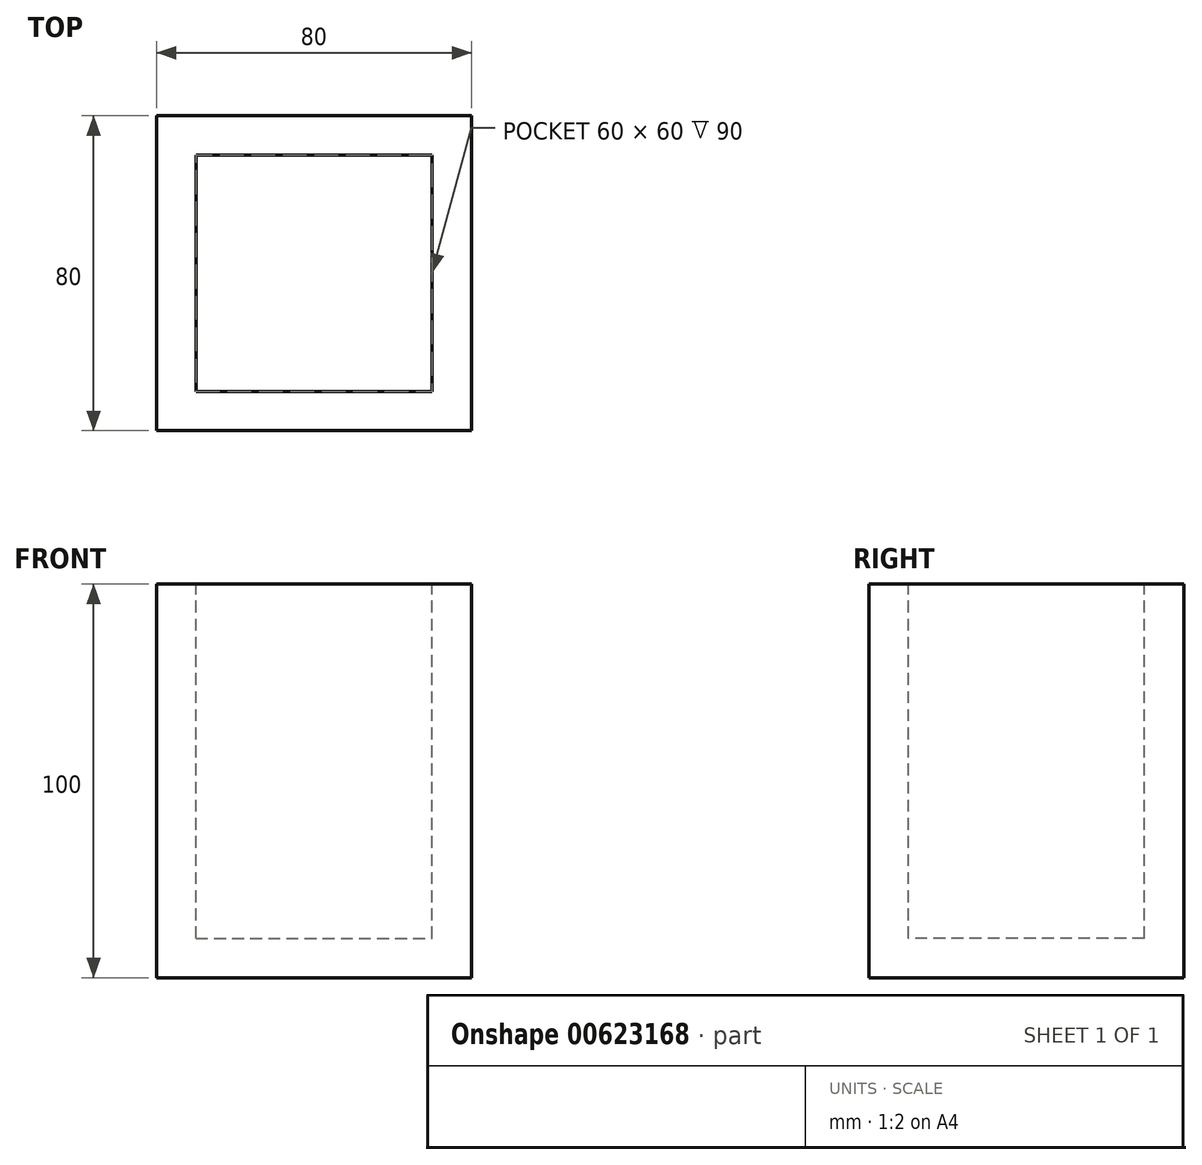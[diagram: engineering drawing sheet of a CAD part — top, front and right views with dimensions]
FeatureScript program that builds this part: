
annotation { "Feature Type Name" : "Feature", "Feature Type Description" : "" }
export const myFeature = defineFeature(function(context is Context, id is Id, definition is map)
    precondition{}
    {
        {
            var Q0;
            Q0=qCreatedBy(makeId("Top.planeOp"),FACE);
            var sketch = newSketch(context, id + "F0", { "sketchPlane" : qUnion([Q0])});
            skLineSegment(sketch, "E0", {"start": v(0, 0) * mm, "end": v(0, 80) * mm});
            skLineSegment(sketch, "E1", {"start": v(0, 80) * mm, "end": v(-80, 80) * mm});
            skLineSegment(sketch, "E2", {"start": v(-80, 80) * mm, "end": v(-80, 0) * mm});
            skLineSegment(sketch, "E3", {"start": v(-80, 0) * mm, "end": v(0, 0) * mm});
            skSolve(sketch);
        }
        {
            var Q0;
            Q0 = qSketchRegion(id + "F0", true);
            extrude(context, id + "F1", {"entities" : qUnion([Q0]), "depth" : 100 * mm, "offsetDistance" : 25 * mm});
        }
        {
            var Q0;
            Q0=makeQuery(id+"F1.opExtrude","CAP_FACE",FACE,{"disambiguationData":[OSD([sQuery(id+"F0.wireOp",EDGE,"E0"),sQuery(id+"F0.wireOp",EDGE,"E1"),sQuery(id+"F0.wireOp",EDGE,"E2"),sQuery(id+"F0.wireOp",EDGE,"E3")])],"isStart":false});
            var sketch = newSketch(context, id + "F2", { "sketchPlane" : qUnion([Q0])});
            skPoint(sketch, "E4", {"position": v(-70, 70) * mm});
            skPoint(sketch, "E5", {"position": v(-10, 70) * mm});
            skPoint(sketch, "E6", {"position": v(-10, 10) * mm});
            skPoint(sketch, "E7", {"position": v(-70, 10) * mm});
            skLineSegment(sketch, "E8", {"start": v(-70, 70) * mm, "end": v(-10, 70) * mm});
            skLineSegment(sketch, "E9", {"start": v(-10, 10) * mm, "end": v(-70, 10) * mm});
            skLineSegment(sketch, "E10", {"start": v(-70, 70) * mm, "end": v(-70, 10) * mm});
            skLineSegment(sketch, "E11", {"start": v(-10, 70) * mm, "end": v(-10, 10) * mm});
            skSolve(sketch);
        }
        {
            var Q0;
            Q0=makeQuery(id+"F2.imprint","IMPRINT",FACE,{"disambiguationData":[TD([[makeQuery(id+"F2.imprint","IMPRINT",EDGE,{"derivedFrom":sQuery(id+"F2.wireOp",EDGE,"E8")}),-1.0]])]});
            extrude(context, id + "F3", {"entities" : qUnion([Q0]), "operationType" : NewBodyOperationType.REMOVE, "oppositeDirection" : true, "depth" : 90 * mm, "offsetDistance" : 25 * mm});
        }
    });
